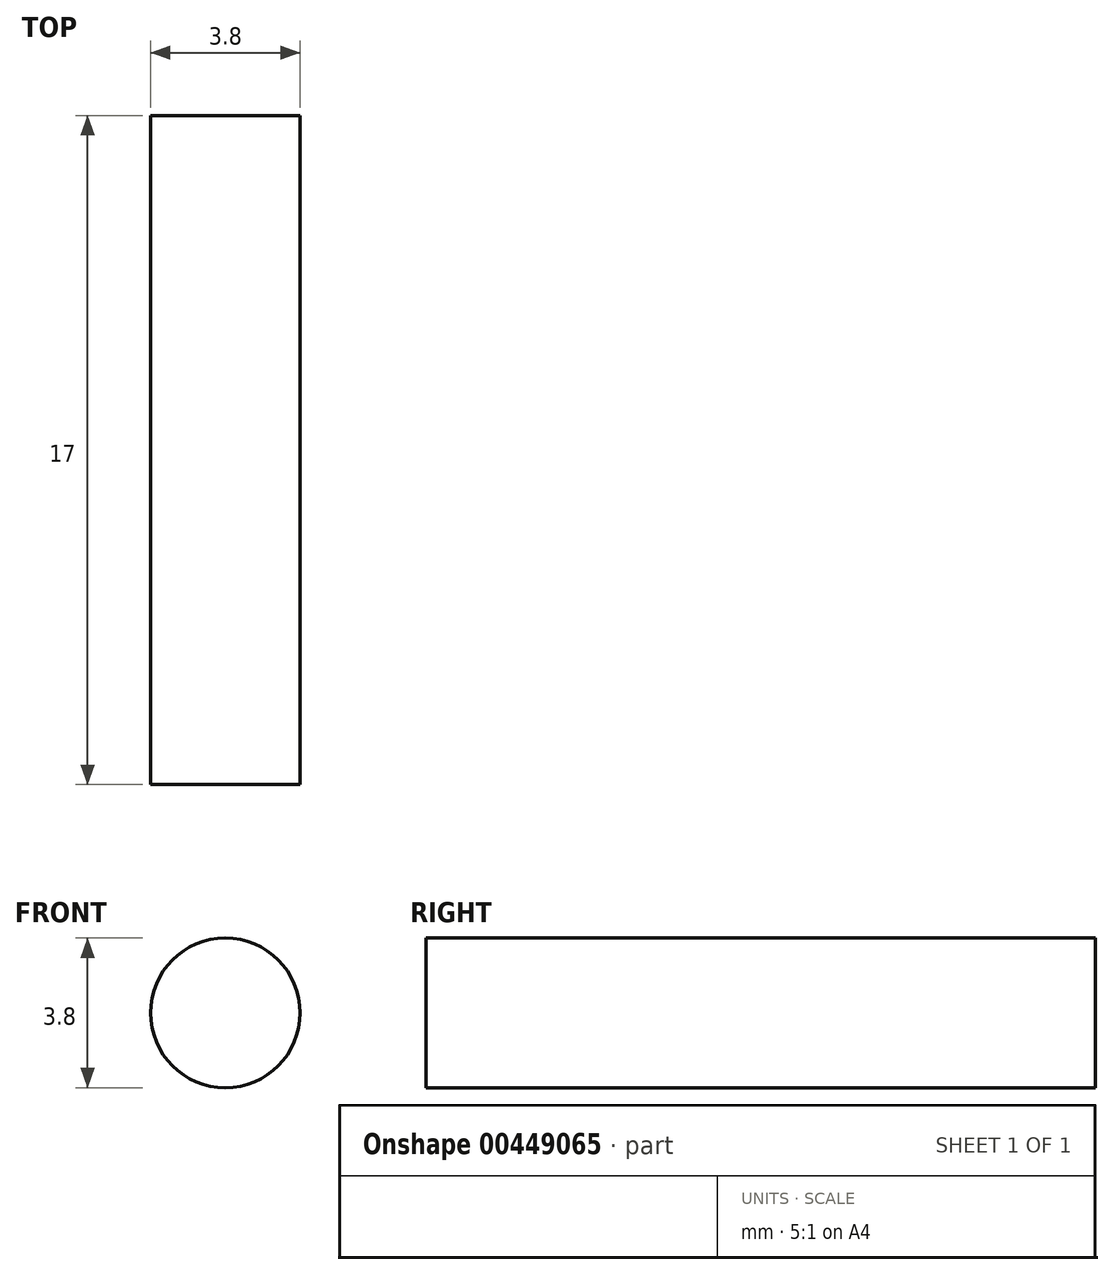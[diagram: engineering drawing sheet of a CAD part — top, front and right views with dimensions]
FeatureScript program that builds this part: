
annotation { "Feature Type Name" : "Feature", "Feature Type Description" : "" }
export const myFeature = defineFeature(function(context is Context, id is Id, definition is map)
    precondition{}
    {
        {
            var Q0;
            Q0=qCreatedBy(makeId("Front.planeOp"),FACE);
            var sketch = newSketch(context, id + "F0", { "sketchPlane" : qUnion([Q0])});
            skCircle(sketch, "E0", {"center": v(0, 0) * mm, "radius": 1.9 * mm});
            skSolve(sketch);
        }
        {
            var Q0;
            Q0=makeQuery(id+"F0.imprint","IMPRINT",FACE,{"disambiguationData":[TD([[makeQuery(id+"F0.imprint","IMPRINT",EDGE,{"derivedFrom":sQuery(id+"F0.wireOp",EDGE,"E0")}),1.0]])]});
            extrude(context, id + "F1", {"entities" : qUnion([Q0]), "depth" : (3 * 5 + 2 * 1) * mm});
        }
    });
